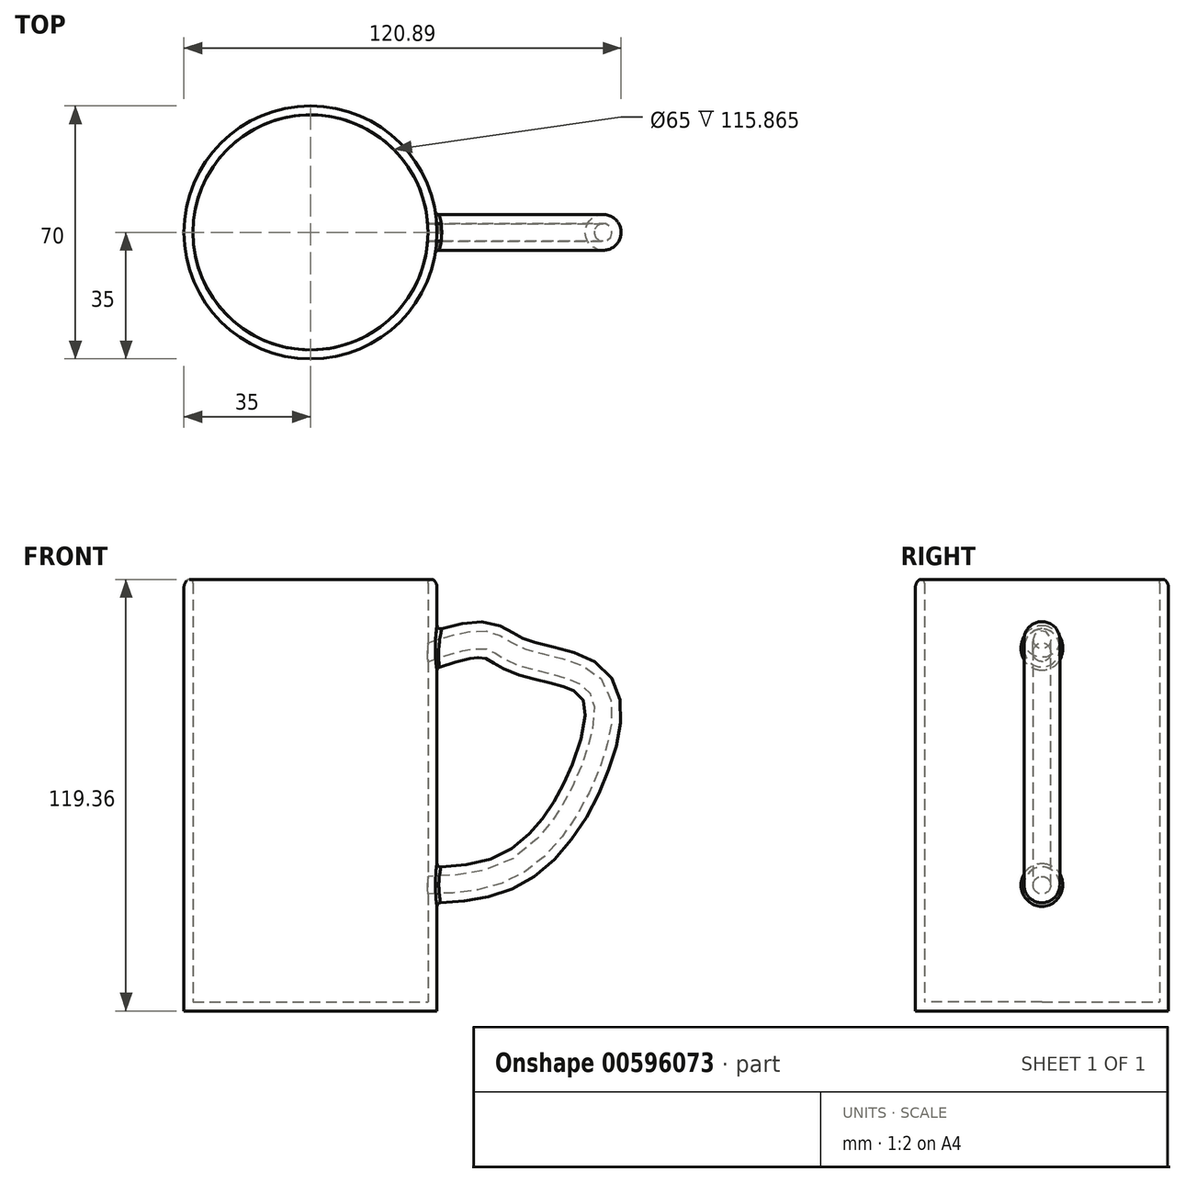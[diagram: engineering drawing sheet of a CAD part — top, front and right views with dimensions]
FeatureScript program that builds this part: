
annotation { "Feature Type Name" : "Feature", "Feature Type Description" : "" }
export const myFeature = defineFeature(function(context is Context, id is Id, definition is map)
    precondition{}
    {
        {
            var Q0;
            Q0=qCreatedBy(makeId("Top.planeOp"),FACE);
            var sketch = newSketch(context, id + "F0", { "sketchPlane" : qUnion([Q0])});
            skCircle(sketch, "E0", {"center": v(0, 0) * mm, "radius": 35 * mm});
            skSolve(sketch);
        }
        {
            var Q0;
            Q0 = qSketchRegion(id + "F0", true);
            extrude(context, id + "F1", {"entities" : qUnion([Q0]), "depth" : 120 * mm, "offsetDistance" : 25 * mm});
        }
        {
            var Q0;
            Q0=qCreatedBy(makeId("Right.planeOp"),FACE);
            cPlane(context, id + "F2", {"entities" : qUnion([Q0]), "cplaneType" : CPlaneType.OFFSET, "offset" : 35 * mm, "width" : 150 * mm, "height" : 150 * mm});
        }
        {
            var Q0;
            Q0=qCreatedBy(makeId("Front.planeOp"),FACE);
            var sketch = newSketch(context, id + "F3", { "sketchPlane" : qUnion([Q0])});
            skFitSpline(sketch, "E1", {"points": [v(26.75, 34.6) * mm, v(57.78, 40.21) * mm, v(78.55, 70.02) * mm, v(78.06, 91.04) * mm, v(57.54, 98.37) * mm, v(48.5, 102.76) * mm, v(24.56, 96.41) * mm], "startDerivative": vector(171.16, 0.19) * mm, "endDerivative": vector(-162.99, -62.85) * mm});
            skSolve(sketch);
        }
        {
            var Q0;
            Q0=qCreatedBy(id+"F2.planeOp",FACE);
            var sketch = newSketch(context, id + "F4", { "sketchPlane" : qUnion([Q0])});
            skCircle(sketch, "E2", {"center": v(0, 34.84) * mm, "radius": 4.94 * mm});
            skSolve(sketch);
        }
        {
            var Q0;
            Q0=makeQuery(id+"F4.imprint","IMPRINT",FACE,{"disambiguationData":[TD([[makeQuery(id+"F4.imprint","IMPRINT",EDGE,{"derivedFrom":sQuery(id+"F4.wireOp",EDGE,"E2")}),1.0]])]});
            var Q1;
            Q1=sQuery(id+"F3.wireOp",EDGE,"E1");
            sweep(context, id + "F5", {"operationType" : NewBodyOperationType.ADD, "profiles" : qUnion([Q0]), "path" : qUnion([Q1])});
        }
        {
            var Q0;
            Q0=makeQuery(id+"F1.opExtrude","CAP_FACE",FACE,{"disambiguationData":[OSD([sQuery(id+"F0.wireOp",EDGE,"E0")])],"isStart":false});
            shell(context, id + "F6", {"entities" : qUnion([Q0]), "thickness" : 2.5 * mm});
        }
        {
            var Q0;
            Q0=makeQuery(id+"F1.opExtrude","CAP_EDGE",EDGE,{"disambiguationData":[OSD([sQuery(id+"F0.wireOp",EDGE,"E0")])],"isStart":false});
            fillet(context, id + "F7", {"entities" : qUnion([Q0]), "radius" : 3 * mm, "tangentPropagation" : true, "allowEdgeOverflow" : false});
        }
        {
            var Q0;
            Q0=makeQuery(id+"F5.boolean.opBoolean","INTERSECT",EDGE,{"disambiguationData":[OD(1.0)],"derivedFrom":[makeQuery(id+"F1.opExtrude","SWEPT_FACE",FACE,{"disambiguationData":[OSD([sQuery(id+"F0.wireOp",EDGE,"E0")])]}),makeQuery(id+"F5.opSweep","SWEPT_FACE",FACE,{"disambiguationData":[OSD([sQuery(id+"F3.wireOp",EDGE,"E1"),sQuery(id+"F4.wireOp",EDGE,"E2")])]})]});
            var Q1;
            Q1=makeQuery(id+"F5.boolean.opBoolean","INTERSECT",EDGE,{"disambiguationData":[OD(0.0)],"derivedFrom":[makeQuery(id+"F1.opExtrude","SWEPT_FACE",FACE,{"disambiguationData":[OSD([sQuery(id+"F0.wireOp",EDGE,"E0")])]}),makeQuery(id+"F5.opSweep","SWEPT_FACE",FACE,{"disambiguationData":[OSD([sQuery(id+"F3.wireOp",EDGE,"E1"),sQuery(id+"F4.wireOp",EDGE,"E2")])]})]});
            var Q2;
            {var subQ0=sQuery(id+"F0.wireOp",EDGE,"E0");Q2=makeQuery(id+"F7.opFillet","BLEND_EDGE",EDGE,{"blendedFrom":[makeQuery(id+"F1.opExtrude","CAP_EDGE",EDGE,{"disambiguationData":[OSD([subQ0])],"isStart":false}),makeQuery(id+"F6.opShell","OFFSET_FACE",FACE,{"disambiguationData":[OSD([subQ0]),TDD([makeQuery(id+"F1.opExtrude","SWEPT_FACE",FACE,{"disambiguationData":[OSD([subQ0])]})])]})],"blendedInto":[makeQuery(id+"F6.opShell","OFFSET_FACE",FACE,{"disambiguationData":[OSD([subQ0]),TDD([makeQuery(id+"F1.opExtrude","SWEPT_FACE",FACE,{"disambiguationData":[OSD([subQ0])]})])]})]});}
            fillet(context, id + "F8", {"entities" : qUnion([Q0, Q1, Q2]), "radius" : 1 * mm, "tangentPropagation" : true, "allowEdgeOverflow" : false});
        }
    });
